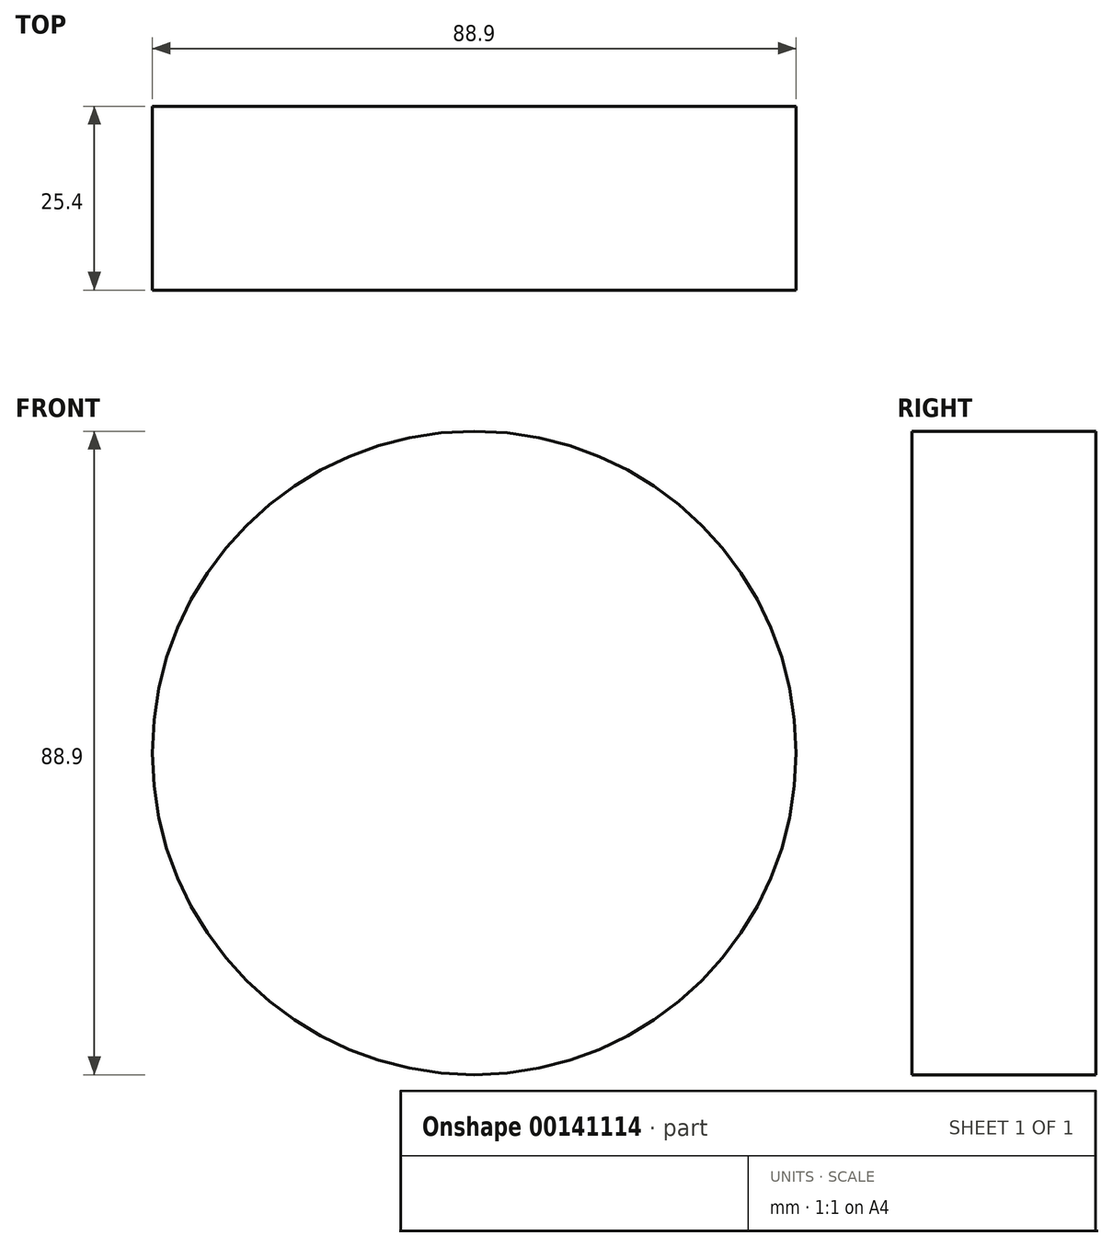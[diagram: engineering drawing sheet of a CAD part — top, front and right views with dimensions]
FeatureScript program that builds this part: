
annotation { "Feature Type Name" : "Feature", "Feature Type Description" : "" }
export const myFeature = defineFeature(function(context is Context, id is Id, definition is map)
    precondition{}
    {
        {
            var Q0;
            Q0=qCreatedBy(makeId("Front.planeOp"),FACE);
            var sketch = newSketch(context, id + "F0", { "sketchPlane" : qUnion([Q0])});
            skCircle(sketch, "E0", {"center": v(0, 0) * mm, "radius": 44.45 * mm});
            skSolve(sketch);
        }
        {
            var Q0;
            Q0 = qSketchRegion(id + "F0", true);
            extrude(context, id + "F1", {"entities" : qUnion([Q0]), "depth" : 25.4 * mm});
        }
    });
